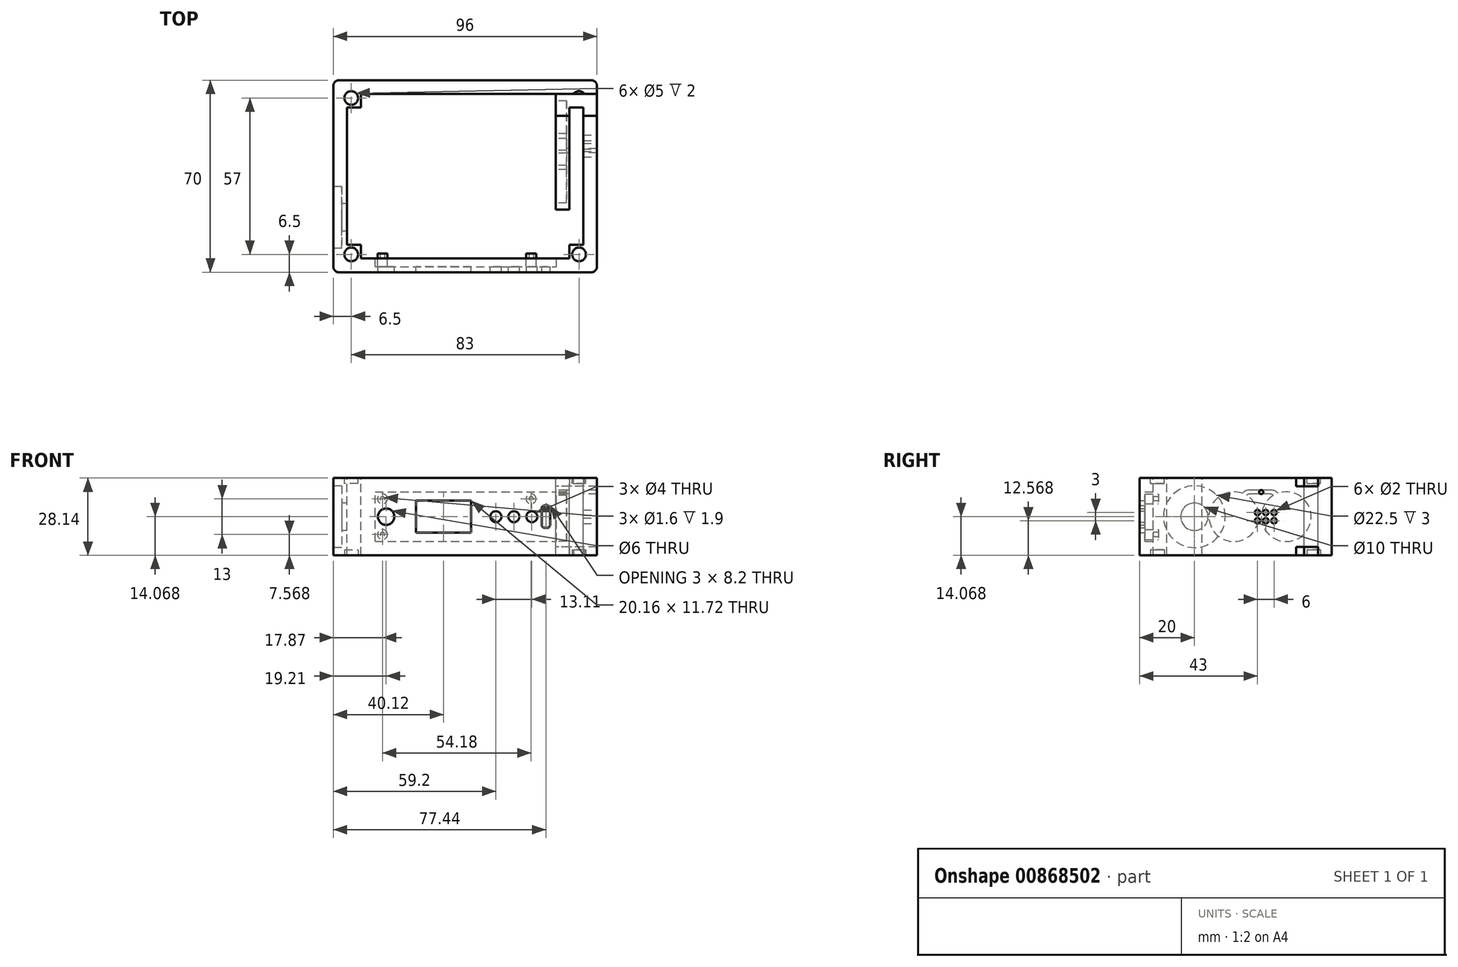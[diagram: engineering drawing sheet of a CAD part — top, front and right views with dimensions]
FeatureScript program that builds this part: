
annotation { "Feature Type Name" : "Feature", "Feature Type Description" : "" }
export const myFeature = defineFeature(function(context is Context, id is Id, definition is map)
    precondition{}
    {
        {
            var Q0;
            Q0=qCreatedBy(makeId("Top.planeOp"),FACE);
            var sketch = newSketch(context, id + "F0", { "sketchPlane" : qUnion([Q0])});
            skLineSegment(sketch, "E0.bottom", {"start": v(-46, 35) * mm, "end": v(46, 35) * mm});
            skLineSegment(sketch, "E0.top", {"start": v(-46, -35) * mm, "end": v(46, -35) * mm});
            skLineSegment(sketch, "E0.left", {"start": v(-48, 33) * mm, "end": v(-48, -33) * mm});
            skLineSegment(sketch, "E0.right", {"start": v(48, 33) * mm, "end": v(48, -33) * mm});
            skPoint(sketch, "E0.middle", {"position": v(0, 0) * mm});
            skPoint(sketch, "E1.visualSharp", {"position": v(-48, 35) * mm});
            skArc(sketch, "E1.filletArc", {"start": v(-46, 35) * mm, "mid": v(-47.41, 34.41) * mm, "end": v(-48, 33) * mm});
            skPoint(sketch, "E2.visualSharp", {"position": v(-48, -35) * mm});
            skArc(sketch, "E2.filletArc", {"start": v(-48, -33) * mm, "mid": v(-47.41, -34.41) * mm, "end": v(-46, -35) * mm});
            skPoint(sketch, "E3.visualSharp", {"position": v(48, -35) * mm});
            skArc(sketch, "E3.filletArc", {"start": v(46, -35) * mm, "mid": v(47.41, -34.41) * mm, "end": v(48, -33) * mm});
            skPoint(sketch, "E4.visualSharp", {"position": v(48, 35) * mm});
            skArc(sketch, "E4.filletArc", {"start": v(48, 33) * mm, "mid": v(47.41, 34.41) * mm, "end": v(46, 35) * mm});
            skSolve(sketch);
        }
        {
            var Q0;
            Q0=makeQuery(id+"F0.imprint","IMPRINT",FACE,{"disambiguationData":[TD([[makeQuery(id+"F0.imprint","IMPRINT",EDGE,{"derivedFrom":sQuery(id+"F0.wireOp",EDGE,"U18dfylj-Norm-gyCY-oxJm-QVkYRqjWbd2D.bottom")}),-1.0]])]});
            var Q1;
            Q1=qSketchRegion(id+"F0",true);
            extrude(context, id + "F1", {"entities" : qUnion([Q0, Q1]), "depth" : 28.14 * mm, "offsetDistance" : 25 * mm});
        }
        {
            var Q0;
            Q0=makeQuery(id+"F1.opExtrude","CAP_FACE",FACE,{"disambiguationData":[OSD([sQuery(id+"F0.wireOp",EDGE,"E0.bottom"),sQuery(id+"F0.wireOp",EDGE,"E0.top"),sQuery(id+"F0.wireOp",EDGE,"E0.left"),sQuery(id+"F0.wireOp",EDGE,"E0.right"),sQuery(id+"F0.wireOp",EDGE,"E1.filletArc"),sQuery(id+"F0.wireOp",EDGE,"E2.filletArc"),sQuery(id+"F0.wireOp",EDGE,"E3.filletArc"),sQuery(id+"F0.wireOp",EDGE,"E4.filletArc")])],"isStart":false});
            var sketch = newSketch(context, id + "F2", { "sketchPlane" : qUnion([Q0])});
            skLineSegment(sketch, "E5.bottom", {"start": v(-44.5, 33) * mm, "end": v(44.5, 33) * mm});
            skLineSegment(sketch, "E5.top", {"start": v(-44.5, -33) * mm, "end": v(44.5, -33) * mm});
            skLineSegment(sketch, "E5.left", {"start": v(-46, 31.5) * mm, "end": v(-46, -31.5) * mm});
            skLineSegment(sketch, "E5.right", {"start": v(46, 31.5) * mm, "end": v(46, -31.5) * mm});
            skPoint(sketch, "E5.middle", {"position": v(0, 0) * mm});
            skPoint(sketch, "E6.visualSharp", {"position": v(-46, 33) * mm});
            skArc(sketch, "E6.filletArc", {"start": v(-44.5, 33) * mm, "mid": v(-45.56, 32.56) * mm, "end": v(-46, 31.5) * mm});
            skPoint(sketch, "E7.visualSharp", {"position": v(46, 33) * mm});
            skArc(sketch, "E7.filletArc", {"start": v(46, 31.5) * mm, "mid": v(45.56, 32.56) * mm, "end": v(44.5, 33) * mm});
            skPoint(sketch, "E8.visualSharp", {"position": v(46, -33) * mm});
            skArc(sketch, "E8.filletArc", {"start": v(44.5, -33) * mm, "mid": v(45.56, -32.56) * mm, "end": v(46, -31.5) * mm});
            skPoint(sketch, "E9.visualSharp", {"position": v(-46, -33) * mm});
            skArc(sketch, "E9.filletArc", {"start": v(-46, -31.5) * mm, "mid": v(-45.56, -32.56) * mm, "end": v(-44.5, -33) * mm});
            skLineSegment(sketch, "E10.bottom", {"start": v(-44, 31.5) * mm, "end": v(44, 31.5) * mm});
            skLineSegment(sketch, "E10.top", {"start": v(-44, -31.5) * mm, "end": v(44, -31.5) * mm});
            skLineSegment(sketch, "E10.left", {"start": v(-44.5, 31) * mm, "end": v(-44.5, -31) * mm});
            skLineSegment(sketch, "E10.right", {"start": v(44.5, 31) * mm, "end": v(44.5, -31) * mm});
            skArc(sketch, "E11.filletArc", {"start": v(-44, 31.5) * mm, "mid": v(-44.35, 31.35) * mm, "end": v(-44.5, 31) * mm});
            skArc(sketch, "E12.filletArc", {"start": v(-44.5, -31) * mm, "mid": v(-44.35, -31.35) * mm, "end": v(-44, -31.5) * mm});
            skArc(sketch, "E13.filletArc", {"start": v(44, -31.5) * mm, "mid": v(44.35, -31.35) * mm, "end": v(44.5, -31) * mm});
            skArc(sketch, "E14.filletArc", {"start": v(44.5, 31) * mm, "mid": v(44.35, 31.35) * mm, "end": v(44, 31.5) * mm});
            skSolve(sketch);
        }
        {
            var Q0;
            Q0=makeQuery(id+"FVReVV0em28uw1l_1.boolean.opBoolean","SPLIT",FACE,{"disambiguationData":[TD([makeQuery(id+"FVReVV0em28uw1l_1.opExtrude","SWEPT_FACE",FACE,{"disambiguationData":[OSD([sQuery(id+"F2.wireOp",EDGE,"E10.bottom")])]})])],"derivedFrom":makeQuery(id+"F1.opExtrude","CAP_FACE",FACE,{"disambiguationData":[OSD([sQuery(id+"F0.wireOp",EDGE,"E0.bottom"),sQuery(id+"F0.wireOp",EDGE,"E0.top"),sQuery(id+"F0.wireOp",EDGE,"E0.left"),sQuery(id+"F0.wireOp",EDGE,"E0.right"),sQuery(id+"F0.wireOp",EDGE,"E1.filletArc"),sQuery(id+"F0.wireOp",EDGE,"E2.filletArc"),sQuery(id+"F0.wireOp",EDGE,"E3.filletArc"),sQuery(id+"F0.wireOp",EDGE,"E4.filletArc")])],"isStart":false})});
            var sketch = newSketch(context, id + "F3", { "sketchPlane" : qUnion([Q0])});
            skCircle(sketch, "E15", {"center": v(-41.5, -28.5) * mm, "radius": 2.5 * mm});
            skCircle(sketch, "E16", {"center": v(-41.5, 28.5) * mm, "radius": 2.5 * mm});
            skCircle(sketch, "E17", {"center": v(41.5, 28.5) * mm, "radius": 2.5 * mm});
            skCircle(sketch, "E18", {"center": v(41.5, -28.5) * mm, "radius": 2.5 * mm});
            skSolve(sketch);
        }
        {
            var Q0;
            Q0=makeQuery(id+"F3.imprint","IMPRINT",FACE,{"disambiguationData":[TD([[makeQuery(id+"F3.imprint","IMPRINT",EDGE,{"derivedFrom":sQuery(id+"F3.wireOp",EDGE,"E15")}),1.0]])]});
            var Q1;
            Q1=makeQuery(id+"F3.imprint","IMPRINT",FACE,{"disambiguationData":[TD([[makeQuery(id+"F3.imprint","IMPRINT",EDGE,{"derivedFrom":sQuery(id+"F3.wireOp",EDGE,"E16")}),1.0]])]});
            var Q2;
            Q2=makeQuery(id+"F3.imprint","IMPRINT",FACE,{"disambiguationData":[TD([[makeQuery(id+"F3.imprint","IMPRINT",EDGE,{"derivedFrom":sQuery(id+"F3.wireOp",EDGE,"E17")}),1.0]])]});
            var Q3;
            Q3=makeQuery(id+"F3.imprint","IMPRINT",FACE,{"disambiguationData":[TD([[makeQuery(id+"F3.imprint","IMPRINT",EDGE,{"derivedFrom":sQuery(id+"F3.wireOp",EDGE,"E18")}),1.0]])]});
            extrude(context, id + "F4", {"entities" : qUnion([Q0, Q1, Q2, Q3]), "operationType" : NewBodyOperationType.REMOVE, "oppositeDirection" : true, "depth" : 2 * mm, "offsetDistance" : 25 * mm});
        }
        {
            var Q0;
            Q0=makeQuery(id+"FVReVV0em28uw1l_1.boolean.opBoolean","SPLIT",FACE,{"disambiguationData":[TD([makeQuery(id+"FVReVV0em28uw1l_1.opExtrude","SWEPT_FACE",FACE,{"disambiguationData":[OSD([sQuery(id+"F2.wireOp",EDGE,"E10.bottom")])]})])],"derivedFrom":makeQuery(id+"F1.opExtrude","CAP_FACE",FACE,{"disambiguationData":[OSD([sQuery(id+"F0.wireOp",EDGE,"E0.bottom"),sQuery(id+"F0.wireOp",EDGE,"E0.top"),sQuery(id+"F0.wireOp",EDGE,"E0.left"),sQuery(id+"F0.wireOp",EDGE,"E0.right"),sQuery(id+"F0.wireOp",EDGE,"E1.filletArc"),sQuery(id+"F0.wireOp",EDGE,"E2.filletArc"),sQuery(id+"F0.wireOp",EDGE,"E3.filletArc"),sQuery(id+"F0.wireOp",EDGE,"E4.filletArc")])],"isStart":false})});
            var sketch = newSketch(context, id + "F5", { "sketchPlane" : qUnion([Q0])});
            skLineSegment(sketch, "E19.bottom", {"start": v(-43, -25) * mm, "end": v(43, -25) * mm});
            skLineSegment(sketch, "E19.top", {"start": v(-43, 25) * mm, "end": v(43, 25) * mm});
            skLineSegment(sketch, "E19.left", {"start": v(-43, -25) * mm, "end": v(-43, 25) * mm});
            skLineSegment(sketch, "E19.right", {"start": v(43, -25) * mm, "end": v(43, 25) * mm});
            skPoint(sketch, "E19.middle", {"position": v(0, 0) * mm});
            skLineSegment(sketch, "E20.bottom", {"start": v(-38, -30) * mm, "end": v(38, -30) * mm});
            skLineSegment(sketch, "E20.top", {"start": v(-38, 30) * mm, "end": v(38, 30) * mm});
            skLineSegment(sketch, "E20.left", {"start": v(-38, -30) * mm, "end": v(-38, 30) * mm});
            skLineSegment(sketch, "E20.right", {"start": v(38, -30) * mm, "end": v(38, 30) * mm});
            skSolve(sketch);
        }
        {
            var Q0;
            {var subQ0=sQuery(id+"F5.wireOp",EDGE,"E19.left");Q0=makeQuery(id+"F5.imprint","IMPRINT",FACE,{"disambiguationData":[TD([[makeQuery(id+"F5.imprint","IMPRINT",EDGE,{"derivedFrom":subQ0}),-1.0]])]});}
            var Q1;
            {var subQ5=sQuery(id+"F5.wireOp",EDGE,"E20.bottom");Q1=makeQuery(id+"F5.imprint","IMPRINT",FACE,{"disambiguationData":[TD([[makeQuery(id+"F5.imprint","IMPRINT",EDGE,{"derivedFrom":subQ5}),1.0]])]});}
            var Q2;
            {var subQ0=sQuery(id+"F5.wireOp",EDGE,"E20.left");var subQ1=sQuery(id+"F5.wireOp",EDGE,"E19.bottom");var subQ2=makeQuery(id+"F5.imprint","INTERSECT",VERTEX,{"derivedFrom":[subQ1,subQ0]});Q2=makeQuery(id+"F5.imprint","IMPRINT",FACE,{"disambiguationData":[TD([[makeQuery(id+"F5.imprint","IMPRINT",EDGE,{"disambiguationData":[TD([[subQ2,-1.0]])],"derivedFrom":subQ1}),1.0]])]});}
            var Q3;
            {var subQ5=sQuery(id+"F5.wireOp",EDGE,"E20.top");Q3=makeQuery(id+"F5.imprint","IMPRINT",FACE,{"disambiguationData":[TD([[makeQuery(id+"F5.imprint","IMPRINT",EDGE,{"derivedFrom":subQ5}),-1.0]])]});}
            var Q4;
            {var subQ0=sQuery(id+"F5.wireOp",EDGE,"E19.right");Q4=makeQuery(id+"F5.imprint","IMPRINT",FACE,{"disambiguationData":[TD([[makeQuery(id+"F5.imprint","IMPRINT",EDGE,{"derivedFrom":subQ0}),1.0]])]});}
            extrude(context, id + "F6", {"entities" : qUnion([Q0, Q1, Q2, Q3, Q4]), "operationType" : NewBodyOperationType.REMOVE, "endBound" : BoundingType.THROUGH_ALL, "oppositeDirection" : true, "depth" : 22 * mm, "offsetDistance" : 25 * mm});
        }
        {
            var Q0;
            Q0=makeQuery(id+"F1.opExtrude","SWEPT_FACE",FACE,{"disambiguationData":[OSD([sQuery(id+"F0.wireOp",EDGE,"E0.right")])]});
            var sketch = newSketch(context, id + "F7", { "sketchPlane" : qUnion([Q0])});
            skPoint(sketch, "E21.centerSnap0", {"position": v(-33, 14.07) * mm});
            skCircle(sketch, "E22", {"center": v(8, 15.57) * mm, "radius": 1 * mm});
            skPoint(sketch, "E22.centerSnap0", {"position": v(0, 0) * mm});
            skCircle(sketch, "E23", {"center": v(11, 15.57) * mm, "radius": 1 * mm});
            skCircle(sketch, "E24", {"center": v(14, 15.57) * mm, "radius": 1 * mm});
            skCircle(sketch, "E25", {"center": v(8, 12.57) * mm, "radius": 1 * mm});
            skCircle(sketch, "E26", {"center": v(11, 12.57) * mm, "radius": 1 * mm});
            skCircle(sketch, "E27", {"center": v(14, 12.57) * mm, "radius": 1 * mm});
            skSolve(sketch);
        }
        {
            var Q0;
            Q0=makeQuery(id+"F7.imprint","IMPRINT",FACE,{"disambiguationData":[TD([[makeQuery(id+"F7.imprint","IMPRINT",EDGE,{"derivedFrom":sQuery(id+"F7.wireOp",EDGE,"E22")}),1.0]])]});
            var Q1;
            Q1=makeQuery(id+"F7.imprint","IMPRINT",FACE,{"disambiguationData":[TD([[makeQuery(id+"F7.imprint","IMPRINT",EDGE,{"derivedFrom":sQuery(id+"F7.wireOp",EDGE,"E25")}),1.0]])]});
            var Q2;
            Q2=makeQuery(id+"F7.imprint","IMPRINT",FACE,{"disambiguationData":[TD([[makeQuery(id+"F7.imprint","IMPRINT",EDGE,{"derivedFrom":sQuery(id+"F7.wireOp",EDGE,"E26")}),1.0]])]});
            var Q3;
            Q3=makeQuery(id+"F7.imprint","IMPRINT",FACE,{"disambiguationData":[TD([[makeQuery(id+"F7.imprint","IMPRINT",EDGE,{"derivedFrom":sQuery(id+"F7.wireOp",EDGE,"E23")}),1.0]])]});
            var Q4;
            Q4=makeQuery(id+"F7.imprint","IMPRINT",FACE,{"disambiguationData":[TD([[makeQuery(id+"F7.imprint","IMPRINT",EDGE,{"derivedFrom":sQuery(id+"F7.wireOp",EDGE,"E24")}),1.0]])]});
            var Q5;
            Q5=makeQuery(id+"F7.imprint","IMPRINT",FACE,{"disambiguationData":[TD([[makeQuery(id+"F7.imprint","IMPRINT",EDGE,{"derivedFrom":sQuery(id+"F7.wireOp",EDGE,"E27")}),1.0]])]});
            extrude(context, id + "F8", {"entities" : qUnion([Q0, Q1, Q2, Q3, Q4, Q5]), "operationType" : NewBodyOperationType.REMOVE, "endBound" : BoundingType.UP_TO_NEXT, "oppositeDirection" : true, "depth" : 25 * mm, "offsetDistance" : 25 * mm});
        }
        {
            var Q0;
            Q0=makeQuery(id+"F1.opExtrude","SWEPT_FACE",FACE,{"disambiguationData":[OSD([sQuery(id+"F0.wireOp",EDGE,"E0.left")])]});
            var sketch = newSketch(context, id + "F9", { "sketchPlane" : qUnion([Q0])});
            skCircle(sketch, "E28", {"center": v(15, 14.07) * mm, "radius": 5 * mm});
            skCircle(sketch, "E29", {"center": v(15, 14.07) * mm, "radius": 11.25 * mm});
            skSolve(sketch);
        }
        {
            var Q0;
            Q0=makeQuery(id+"F9.imprint","IMPRINT",FACE,{"disambiguationData":[TD([[makeQuery(id+"F9.imprint","IMPRINT",EDGE,{"derivedFrom":sQuery(id+"F9.wireOp",EDGE,"E28")}),-1.0]])]});
            extrude(context, id + "F10", {"entities" : qUnion([Q0]), "operationType" : NewBodyOperationType.REMOVE, "oppositeDirection" : true, "depth" : 3 * mm, "offsetDistance" : 25 * mm});
        }
        {
            var Q0;
            Q0=makeQuery(id+"F9.imprint","IMPRINT",FACE,{"disambiguationData":[TD([[makeQuery(id+"F9.imprint","IMPRINT",EDGE,{"derivedFrom":sQuery(id+"F9.wireOp",EDGE,"E28")}),1.0]])]});
            extrude(context, id + "F11", {"entities" : qUnion([Q0]), "operationType" : NewBodyOperationType.REMOVE, "endBound" : BoundingType.UP_TO_NEXT, "oppositeDirection" : true, "depth" : 25 * mm, "offsetDistance" : 25 * mm});
        }
        {
            var Q0;
            Q0=makeQuery(id+"F6.boolean.opBoolean","COPY",FACE,{"derivedFrom":makeQuery(id+"F6.opExtrude","SWEPT_FACE",FACE,{"disambiguationData":[OSD([sQuery(id+"F5.wireOp",EDGE,"E20.bottom")])]})});
            var sketch = newSketch(context, id + "F12", { "sketchPlane" : qUnion([Q0])});
            skLineSegment(sketch, "E30.bottom", {"start": v(32.79, 5.07) * mm, "end": v(-33.21, 5.07) * mm});
            skLineSegment(sketch, "E30.top", {"start": v(32.79, 23.07) * mm, "end": v(-33.21, 23.07) * mm});
            skLineSegment(sketch, "E30.left", {"start": v(32.79, 5.07) * mm, "end": v(32.79, 23.07) * mm});
            skLineSegment(sketch, "E30.right", {"start": v(-33.21, 5.07) * mm, "end": v(-33.21, 23.07) * mm});
            skPoint(sketch, "E30.middle", {"position": v(-0.21, 14.07) * mm});
            skPoint(sketch, "E30.middle.positionSnap0", {"position": v(45.84, 14.07) * mm});
            skPoint(sketch, "E30.centerSnap0", {"position": v(45.84, 14.07) * mm});
            skLineSegment(sketch, "E31.bottom", {"start": v(-29.94, 9.97) * mm, "end": v(-28.94, 9.97) * mm});
            skLineSegment(sketch, "E31.top", {"start": v(-29.94, 18.17) * mm, "end": v(-28.94, 18.17) * mm});
            skLineSegment(sketch, "E31.left", {"start": v(-30.94, 10.97) * mm, "end": v(-30.94, 17.17) * mm});
            skLineSegment(sketch, "E31.right", {"start": v(-27.94, 10.97) * mm, "end": v(-27.94, 17.17) * mm});
            skPoint(sketch, "E31.middle", {"position": v(-29.44, 14.07) * mm});
            skPoint(sketch, "E31.middle.positionSnap0", {"position": v(-33.21, 14.07) * mm});
            skPoint(sketch, "E31.centerSnap0", {"position": v(-33.21, 14.07) * mm});
            skPoint(sketch, "E32.visualSharp", {"position": v(-27.94, 18.17) * mm});
            skArc(sketch, "E32.filletArc", {"start": v(-27.94, 17.17) * mm, "mid": v(-28.23, 17.87) * mm, "end": v(-28.94, 18.17) * mm});
            skPoint(sketch, "E33.visualSharp", {"position": v(-27.94, 9.97) * mm});
            skArc(sketch, "E33.filletArc", {"start": v(-28.94, 9.97) * mm, "mid": v(-28.23, 10.26) * mm, "end": v(-27.94, 10.97) * mm});
            skPoint(sketch, "E34.visualSharp", {"position": v(-30.94, 9.97) * mm});
            skArc(sketch, "E34.filletArc", {"start": v(-30.94, 10.97) * mm, "mid": v(-30.65, 10.26) * mm, "end": v(-29.94, 9.97) * mm});
            skPoint(sketch, "E35.visualSharp", {"position": v(-30.94, 18.17) * mm});
            skArc(sketch, "E35.filletArc", {"start": v(-29.94, 18.17) * mm, "mid": v(-30.65, 17.87) * mm, "end": v(-30.94, 17.17) * mm});
            skCircle(sketch, "E36", {"center": v(-24.31, 14.07) * mm, "radius": 2 * mm});
            skCircle(sketch, "E37", {"center": v(-17.76, 14.07) * mm, "radius": 2 * mm});
            skCircle(sketch, "E38", {"center": v(-11.2, 14.07) * mm, "radius": 2 * mm});
            skCircle(sketch, "E39", {"center": v(28.79, 14.07) * mm, "radius": 3 * mm});
            skCircle(sketch, "E40", {"center": v(30.13, 20.57) * mm, "radius": 1.8 * mm});
            skCircle(sketch, "E41", {"center": v(30.13, 20.57) * mm, "radius": 0.8 * mm});
            skCircle(sketch, "E42", {"center": v(30.13, 7.57) * mm, "radius": 1.8 * mm});
            skCircle(sketch, "E43", {"center": v(30.13, 7.57) * mm, "radius": 0.8 * mm});
            skLineSegment(sketch, "E44.bottom", {"start": v(-2.2, 19.93) * mm, "end": v(17.96, 19.93) * mm});
            skLineSegment(sketch, "E44.top", {"start": v(-2.2, 8.2) * mm, "end": v(17.96, 8.2) * mm});
            skLineSegment(sketch, "E44.left", {"start": v(-2.2, 19.93) * mm, "end": v(-2.2, 8.2) * mm});
            skLineSegment(sketch, "E44.right", {"start": v(17.96, 19.93) * mm, "end": v(17.96, 8.2) * mm});
            skPoint(sketch, "E44.middle", {"position": v(7.88, 14.07) * mm});
            skCircle(sketch, "E45", {"center": v(-24.05, 20.57) * mm, "radius": 1.8 * mm});
            skCircle(sketch, "E46", {"center": v(-24.05, 20.57) * mm, "radius": 0.8 * mm});
            skSolve(sketch);
        }
        {
            var Q0;
            Q0=makeQuery(id+"F12.imprint","IMPRINT",FACE,{"disambiguationData":[TD([[makeQuery(id+"F12.imprint","IMPRINT",EDGE,{"derivedFrom":sQuery(id+"F12.wireOp",EDGE,"E44.bottom")}),-1.0]])]});
            var Q1;
            Q1=makeQuery(id+"F12.imprint","IMPRINT",FACE,{"disambiguationData":[TD([[makeQuery(id+"F12.imprint","IMPRINT",EDGE,{"derivedFrom":sQuery(id+"F12.wireOp",EDGE,"E39")}),1.0]])]});
            var Q2;
            Q2=makeQuery(id+"F12.imprint","IMPRINT",FACE,{"disambiguationData":[TD([[makeQuery(id+"F12.imprint","IMPRINT",EDGE,{"derivedFrom":sQuery(id+"F12.wireOp",EDGE,"E38")}),1.0]])]});
            var Q3;
            Q3=makeQuery(id+"F12.imprint","IMPRINT",FACE,{"disambiguationData":[TD([[makeQuery(id+"F12.imprint","IMPRINT",EDGE,{"derivedFrom":sQuery(id+"F12.wireOp",EDGE,"E37")}),1.0]])]});
            var Q4;
            Q4=makeQuery(id+"F12.imprint","IMPRINT",FACE,{"disambiguationData":[TD([[makeQuery(id+"F12.imprint","IMPRINT",EDGE,{"derivedFrom":sQuery(id+"F12.wireOp",EDGE,"E36")}),1.0]])]});
            var Q5;
            Q5=makeQuery(id+"F12.imprint","IMPRINT",FACE,{"disambiguationData":[TD([[makeQuery(id+"F12.imprint","IMPRINT",EDGE,{"derivedFrom":sQuery(id+"F12.wireOp",EDGE,"E31.bottom")}),1.0]])]});
            extrude(context, id + "F13", {"entities" : qUnion([Q0, Q1, Q2, Q3, Q4, Q5]), "operationType" : NewBodyOperationType.REMOVE, "endBound" : BoundingType.UP_TO_NEXT, "oppositeDirection" : true, "depth" : 25 * mm, "offsetDistance" : 25 * mm});
        }
        {
            var Q0;
            Q0=makeQuery(id+"F12.imprint","IMPRINT",FACE,{"disambiguationData":[TD([[makeQuery(id+"F12.imprint","IMPRINT",EDGE,{"derivedFrom":sQuery(id+"F12.wireOp",EDGE,"E30.bottom")}),-1.0]])]});
            extrude(context, id + "F14", {"entities" : qUnion([Q0]), "operationType" : NewBodyOperationType.REMOVE, "oppositeDirection" : true, "depth" : -3 * mm, "offsetDistance" : 25 * mm});
        }
        {
            var Q0;
            Q0=makeQuery(id+"F12.imprint","IMPRINT",FACE,{"disambiguationData":[TD([[makeQuery(id+"F12.imprint","IMPRINT",EDGE,{"derivedFrom":sQuery(id+"F12.wireOp",EDGE,"E30.bottom")}),-1.0]])]});
            extrude(context, id + "F15", {"entities" : qUnion([Q0]), "operationType" : NewBodyOperationType.REMOVE, "oppositeDirection" : true, "depth" : 3 * mm, "offsetDistance" : 25 * mm});
        }
        {
            var Q0;
            Q0=makeQuery(id+"F12.imprint","IMPRINT",FACE,{"disambiguationData":[TD([[makeQuery(id+"F12.imprint","IMPRINT",EDGE,{"derivedFrom":sQuery(id+"F12.wireOp",EDGE,"E40")}),1.0]])]});
            var Q1;
            Q1=sQuery(id+"F12.wireOp",EDGE,"E41");
            var Q2;
            Q2=sQuery(id+"F12.wireOp",EDGE,"E40");
            extrude(context, id + "F16", {"entities" : qUnion([Q0]), "operationType" : NewBodyOperationType.ADD, "surfaceEntities" : qUnion([Q1, Q2]), "depth" : 1.9 * mm, "offsetDistance" : 25 * mm});
        }
        {
            var Q0;
            Q0=makeQuery(id+"F12.imprint","IMPRINT",FACE,{"disambiguationData":[TD([[makeQuery(id+"F12.imprint","IMPRINT",EDGE,{"derivedFrom":sQuery(id+"F12.wireOp",EDGE,"E42")}),1.0]])]});
            var Q1;
            Q1=sQuery(id+"F12.wireOp",EDGE,"E43");
            var Q2;
            Q2=sQuery(id+"F12.wireOp",EDGE,"E42");
            extrude(context, id + "F17", {"entities" : qUnion([Q0]), "operationType" : NewBodyOperationType.ADD, "surfaceEntities" : qUnion([Q1, Q2]), "depth" : 1.9 * mm, "offsetDistance" : 25 * mm});
        }
        {
            var Q0;
            Q0=makeQuery(id+"F12.imprint","IMPRINT",FACE,{"disambiguationData":[TD([[makeQuery(id+"F12.imprint","IMPRINT",EDGE,{"derivedFrom":sQuery(id+"F12.wireOp",EDGE,"E45")}),1.0]])]});
            extrude(context, id + "F18", {"entities" : qUnion([Q0]), "operationType" : NewBodyOperationType.ADD, "depth" : 1.9 * mm, "offsetDistance" : 25 * mm});
        }
        {
            var Q0;
            Q0=makeQuery(id+"F1.opExtrude","CAP_FACE",FACE,{"disambiguationData":[OSD([sQuery(id+"F0.wireOp",EDGE,"E0.bottom"),sQuery(id+"F0.wireOp",EDGE,"E0.top"),sQuery(id+"F0.wireOp",EDGE,"E0.left"),sQuery(id+"F0.wireOp",EDGE,"E0.right"),sQuery(id+"F0.wireOp",EDGE,"E1.filletArc"),sQuery(id+"F0.wireOp",EDGE,"E2.filletArc"),sQuery(id+"F0.wireOp",EDGE,"E3.filletArc"),sQuery(id+"F0.wireOp",EDGE,"E4.filletArc")])],"isStart":true});
            var sketch = newSketch(context, id + "F19", { "sketchPlane" : qUnion([Q0])});
            skCircle(sketch, "E47", {"center": v(-41.5, -28.5) * mm, "radius": 2.5 * mm});
            skCircle(sketch, "E48", {"center": v(-41.5, 28.5) * mm, "radius": 2.5 * mm});
            skCircle(sketch, "E49", {"center": v(41.5, -28.5) * mm, "radius": 2.5 * mm});
            skCircle(sketch, "E50", {"center": v(41.5, 28.5) * mm, "radius": 2.5 * mm});
            skSolve(sketch);
        }
        {
            var Q0;
            Q0=makeQuery(id+"F19.imprint","IMPRINT",FACE,{"disambiguationData":[TD([[makeQuery(id+"F19.imprint","IMPRINT",EDGE,{"derivedFrom":sQuery(id+"F19.wireOp",EDGE,"E47")}),1.0]])]});
            var Q1;
            Q1=makeQuery(id+"F19.imprint","IMPRINT",FACE,{"disambiguationData":[TD([[makeQuery(id+"F19.imprint","IMPRINT",EDGE,{"derivedFrom":sQuery(id+"F19.wireOp",EDGE,"E48")}),1.0]])]});
            var Q2;
            Q2=makeQuery(id+"F19.imprint","IMPRINT",FACE,{"disambiguationData":[TD([[makeQuery(id+"F19.imprint","IMPRINT",EDGE,{"derivedFrom":sQuery(id+"F19.wireOp",EDGE,"E49")}),1.0]])]});
            var Q3;
            Q3=makeQuery(id+"F19.imprint","IMPRINT",FACE,{"disambiguationData":[TD([[makeQuery(id+"F19.imprint","IMPRINT",EDGE,{"derivedFrom":sQuery(id+"F19.wireOp",EDGE,"E50")}),1.0]])]});
            var Q4;
            Q4=sQuery(id+"F19.wireOp",EDGE,"E47");
            var Q5;
            Q5=sQuery(id+"F19.wireOp",EDGE,"E48");
            var Q6;
            Q6=sQuery(id+"F19.wireOp",EDGE,"E49");
            var Q7;
            Q7=sQuery(id+"F19.wireOp",EDGE,"E50");
            extrude(context, id + "F20", {"entities" : qUnion([Q0, Q1, Q2, Q3]), "operationType" : NewBodyOperationType.REMOVE, "surfaceEntities" : qUnion([Q4, Q5, Q6, Q7]), "oppositeDirection" : true, "depth" : 2 * mm, "offsetDistance" : 25 * mm});
        }
        {
            var Q0;
            {var subQ0=sQuery(id+"F5.wireOp",EDGE,"E20.right");Q0=makeQuery(id+"F6.boolean.opBoolean","COPY",FACE,{"derivedFrom":makeQuery(id+"F6.opExtrude","SWEPT_FACE",FACE,{"disambiguationData":[OSD([subQ0]),TDD([makeQuery(id+"F5.imprint","IMPRINT",EDGE,{"disambiguationData":[TD([[makeQuery(id+"F5.imprint","INTERSECT",VERTEX,{"derivedFrom":[sQuery(id+"F5.wireOp",EDGE,"E20.top"),subQ0]}),1.0]])],"derivedFrom":subQ0})])]})});}
            extrude(context, id + "F21", {"entities" : qUnion([Q0]), "depth" : 3 * mm, "offsetDistance" : 25 * mm});
        }
        {
            var Q0;
            Q0=makeQuery(id+"F21.opExtrude","SWEPT_FACE",FACE,{"disambiguationData":[OSD([sQuery(id+"F5.wireOp",EDGE,"E19.top"),sQuery(id+"F5.wireOp",EDGE,"E20.right")])]});
            extrude(context, id + "F22", {"entities" : qUnion([Q0]), "operationType" : NewBodyOperationType.ADD, "depth" : 37.2 * mm, "offsetDistance" : 25 * mm});
        }
        {
            var Q0;
            {var subQ0=sQuery(id+"F5.wireOp",EDGE,"E20.right");var subQ1=sQuery(id+"F5.wireOp",EDGE,"E19.top");Q0=makeQuery(id+"F22.boolean.opBoolean","MERGE",FACE,{"derivedFrom":[makeQuery(id+"F21.opExtrude","CAP_FACE",FACE,{"disambiguationData":[OSD([subQ0])],"isStart":false}),makeQuery(id+"F22.opExtrude","SWEPT_FACE",FACE,{"disambiguationData":[OSD([subQ1,subQ0]),TDD([makeQuery(id+"F21.opExtrude","CAP_EDGE",EDGE,{"disambiguationData":[OSD([subQ1,subQ0])],"isStart":false})])]})]});}
            var sketch = newSketch(context, id + "F23", { "sketchPlane" : qUnion([Q0])});
            skCircle(sketch, "E51", {"center": v(-18.45, 14.07) * mm, "radius": 9.05 * mm});
            skCircle(sketch, "E52", {"center": v(0.65, 14.07) * mm, "radius": 9.05 * mm});
            skSolve(sketch);
        }
        {
            var Q0;
            Q0=makeQuery(id+"F23.imprint","IMPRINT",FACE,{"disambiguationData":[TD([[makeQuery(id+"F23.imprint","IMPRINT",EDGE,{"derivedFrom":sQuery(id+"F23.wireOp",EDGE,"E51")}),1.0]])]});
            var Q1;
            Q1=makeQuery(id+"F23.imprint","IMPRINT",FACE,{"disambiguationData":[TD([[makeQuery(id+"F23.imprint","IMPRINT",EDGE,{"derivedFrom":sQuery(id+"F23.wireOp",EDGE,"E52")}),1.0]])]});
            extrude(context, id + "F24", {"entities" : qUnion([Q0, Q1]), "operationType" : NewBodyOperationType.REMOVE, "oppositeDirection" : true, "depth" : 2 * mm, "offsetDistance" : 25 * mm});
        }
        {
            var Q0;
            {var subQ0=sQuery(id+"F5.wireOp",EDGE,"E20.right");var subQ1=sQuery(id+"F5.wireOp",EDGE,"E19.top");Q0=makeQuery(id+"F22.boolean.opBoolean","MERGE",FACE,{"derivedFrom":[makeQuery(id+"F21.opExtrude","CAP_FACE",FACE,{"disambiguationData":[OSD([subQ0])],"isStart":false}),makeQuery(id+"F22.opExtrude","SWEPT_FACE",FACE,{"disambiguationData":[OSD([subQ1,subQ0]),TDD([makeQuery(id+"F21.opExtrude","CAP_EDGE",EDGE,{"disambiguationData":[OSD([subQ1,subQ0])],"isStart":false})])]})]});}
            var sketch = newSketch(context, id + "F25", { "sketchPlane" : qUnion([Q0])});
            skLineSegment(sketch, "E53", {"start": v(-22, 0) * mm, "end": v(-22, 3) * mm});
            skLineSegment(sketch, "E54", {"start": v(-22, 3) * mm, "end": v(-30, 3) * mm});
            skLineSegment(sketch, "E55", {"start": v(-22, 25.14) * mm, "end": v(-22, 28.14) * mm});
            skLineSegment(sketch, "E56", {"start": v(-22, 25.14) * mm, "end": v(-30, 25.14) * mm});
            skCircle(sketch, "E57", {"center": v(-18.45, 14.07) * mm, "radius": 3 * mm});
            skCircle(sketch, "E58", {"center": v(0.65, 14.07) * mm, "radius": 3 * mm});
            skSolve(sketch);
        }
        {
            var Q0;
            {var subQ0=sQuery(id+"F25.wireOp",EDGE,"E53");Q0=makeQuery(id+"F25.imprint","IMPRINT",FACE,{"disambiguationData":[TD([[makeQuery(id+"F25.imprint","IMPRINT",EDGE,{"derivedFrom":subQ0}),1.0]])]});}
            var Q1;
            {var subQ0=sQuery(id+"F25.wireOp",EDGE,"E55");Q1=makeQuery(id+"F25.imprint","IMPRINT",FACE,{"disambiguationData":[TD([[makeQuery(id+"F25.imprint","IMPRINT",EDGE,{"derivedFrom":subQ0}),1.0]])]});}
            var Q2;
            {var subQ0=sQuery(id+"F25.wireOp",EDGE,"vlVvI3g9-1gb2-cv2B-r6I6-xqho5fVS6g8k");Q2=makeQuery(id+"F25.imprint","IMPRINT",FACE,{"disambiguationData":[TD([[makeQuery(id+"F25.imprint","IMPRINT",EDGE,{"derivedFrom":subQ0}),-1.0]])]});}
            var Q3;
            {var subQ0=sQuery(id+"F25.wireOp",EDGE,"rPsMb9RV-sWKV-OP7q-Go8H-27vObzox9KDB");Q3=makeQuery(id+"F25.imprint","IMPRINT",FACE,{"disambiguationData":[TD([[makeQuery(id+"F25.imprint","IMPRINT",EDGE,{"derivedFrom":subQ0}),1.0]])]});}
            extrude(context, id + "F26", {"entities" : qUnion([Q0, Q1, Q2, Q3]), "operationType" : NewBodyOperationType.REMOVE, "oppositeDirection" : true, "depth" : 25 * mm, "offsetDistance" : 25 * mm});
        }
        {
            var Q0;
            {var subQ0=sQuery(id+"F5.wireOp",EDGE,"E20.right");var subQ1=sQuery(id+"F5.wireOp",EDGE,"E19.top");Q0=makeQuery(id+"F22.boolean.opBoolean","MERGE",FACE,{"derivedFrom":[makeQuery(id+"F21.opExtrude","CAP_FACE",FACE,{"disambiguationData":[OSD([subQ0])],"isStart":false}),makeQuery(id+"F22.opExtrude","SWEPT_FACE",FACE,{"disambiguationData":[OSD([subQ1,subQ0]),TDD([makeQuery(id+"F21.opExtrude","CAP_EDGE",EDGE,{"disambiguationData":[OSD([subQ1,subQ0])],"isStart":false})])]})]});}
            var sketch = newSketch(context, id + "F27", { "sketchPlane" : qUnion([Q0])});
            skLineSegment(sketch, "E59", {"start": v(-12.68, 22.3) * mm, "end": v(-5.12, 22.3) * mm});
            skArc(sketch, "E60", {"start": v(-12.68, 22.3) * mm, "mid": v(-13.28, 22.17) * mm, "end": v(-13.78, 21.82) * mm});
            skArc(sketch, "E61", {"start": v(-4.02, 21.82) * mm, "mid": v(-4.52, 22.17) * mm, "end": v(-5.12, 22.3) * mm});
            skLineSegment(sketch, "E62", {"start": v(-12.68, 23.8) * mm, "end": v(-5.12, 23.8) * mm});
            skArc(sketch, "E63", {"start": v(-12.68, 23.8) * mm, "mid": v(-14.22, 23.5) * mm, "end": v(-15.53, 22.63) * mm});
            skArc(sketch, "E64", {"start": v(-2.45, 22.57) * mm, "mid": v(-3.65, 23.47) * mm, "end": v(-5.12, 23.8) * mm});
            skCircle(sketch, "E65", {"center": v(-9.34, 23.05) * mm, "radius": 0.75 * mm});
            skSolve(sketch);
        }
        {
            var Q0;
            {var subQ0=sQuery(id+"F27.wireOp",EDGE,"E65");var subQ1=makeQuery(id+"F27.imprint","INTERSECT",VERTEX,{"derivedFrom":[sQuery(id+"F27.wireOp",EDGE,"E59"),subQ0]});Q0=makeQuery(id+"F27.imprint","IMPRINT",FACE,{"disambiguationData":[TD([[makeQuery(id+"F27.imprint","IMPRINT",EDGE,{"disambiguationData":[TD([[subQ1,1.0]])],"derivedFrom":subQ0}),1.0]])]});}
            extrude(context, id + "F28", {"entities" : qUnion([Q0]), "operationType" : NewBodyOperationType.REMOVE, "oppositeDirection" : true, "depth" : 25 * mm, "offsetDistance" : 25 * mm});
        }
        {
            var Q0;
            {var subQ4=sQuery(id+"F27.wireOp",EDGE,"E60");Q0=makeQuery(id+"F27.imprint","IMPRINT",FACE,{"disambiguationData":[TD([[makeQuery(id+"F27.imprint","IMPRINT",EDGE,{"derivedFrom":subQ4}),-1.0]])]});}
            var Q1;
            {var subQ4=sQuery(id+"F27.wireOp",EDGE,"E61");Q1=makeQuery(id+"F27.imprint","IMPRINT",FACE,{"disambiguationData":[TD([[makeQuery(id+"F27.imprint","IMPRINT",EDGE,{"derivedFrom":subQ4}),-1.0]])]});}
            extrude(context, id + "F29", {"entities" : qUnion([Q0, Q1]), "operationType" : NewBodyOperationType.REMOVE, "oppositeDirection" : true, "depth" : 2 * mm, "offsetDistance" : 25 * mm});
        }
        {
            var Q0;
            {var subQ0=sQuery(id+"F5.wireOp",EDGE,"E20.right");var subQ1=sQuery(id+"F5.wireOp",EDGE,"E19.top");Q0=makeQuery(id+"F22.boolean.opBoolean","MERGE",FACE,{"derivedFrom":[makeQuery(id+"F21.opExtrude","CAP_FACE",FACE,{"disambiguationData":[OSD([subQ0])],"isStart":false}),makeQuery(id+"F22.opExtrude","SWEPT_FACE",FACE,{"disambiguationData":[OSD([subQ1,subQ0]),TDD([makeQuery(id+"F21.opExtrude","CAP_EDGE",EDGE,{"disambiguationData":[OSD([subQ1,subQ0])],"isStart":false})])]})]});}
            extrude(context, id + "F30", {"entities" : qUnion([Q0]), "operationType" : NewBodyOperationType.ADD, "depth" : 2 * mm, "offsetDistance" : 25 * mm});
        }
    });
